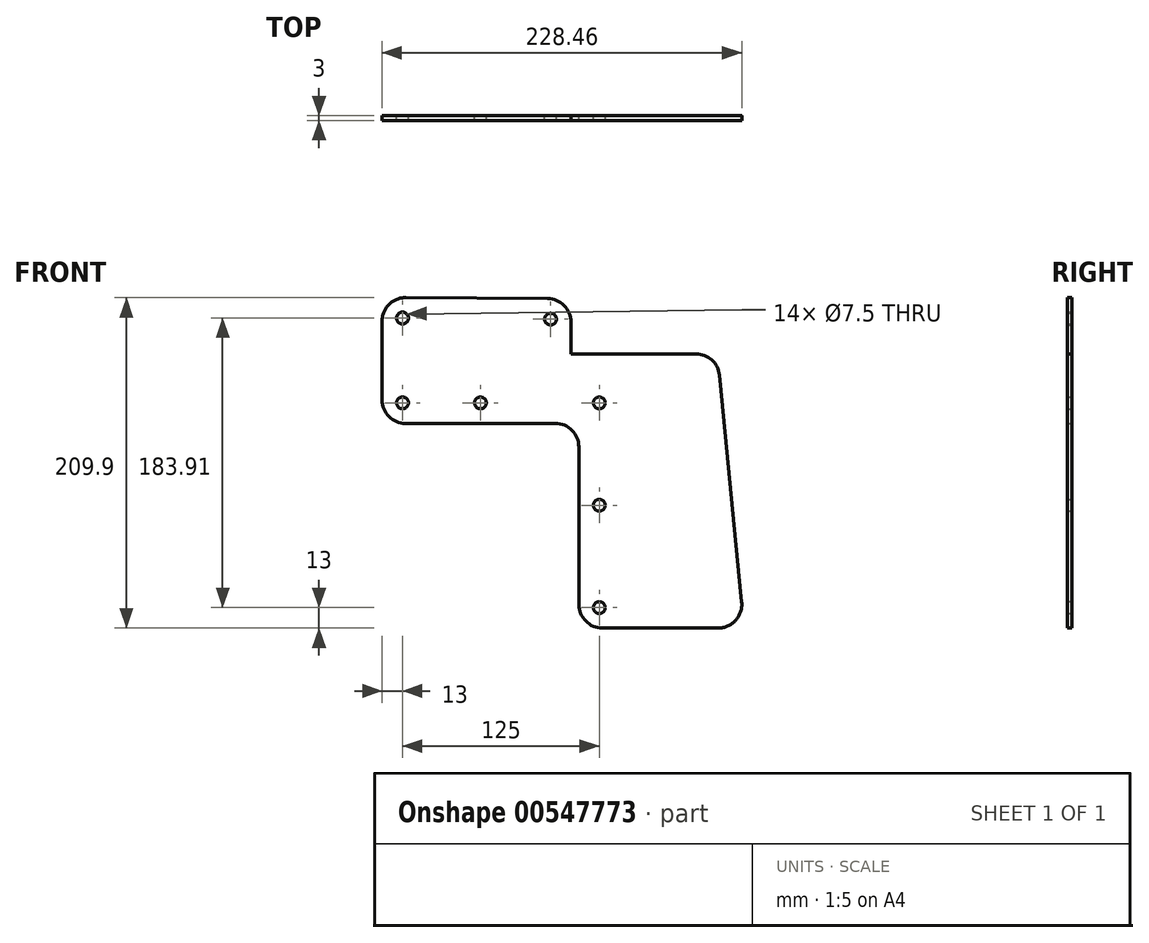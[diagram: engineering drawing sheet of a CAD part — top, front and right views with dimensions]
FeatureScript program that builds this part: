
annotation { "Feature Type Name" : "Feature", "Feature Type Description" : "" }
export const myFeature = defineFeature(function(context is Context, id is Id, definition is map)
    precondition{}
    {
        {
            var Q0;
            Q0=qCreatedBy(makeId("Front.planeOp"),FACE);
            var sketch = newSketch(context, id + "F0", { "sketchPlane" : qUnion([Q0])});
            skLineSegment(sketch, "E0", {"start": v(0, -15.1) * mm, "end": v(0, -65) * mm});
            skLineSegment(sketch, "E1", {"start": v(15, -80) * mm, "end": v(110, -80) * mm});
            skLineSegment(sketch, "E2", {"start": v(125, -95) * mm, "end": v(125, -195) * mm});
            skLineSegment(sketch, "E3", {"start": v(140, -210) * mm, "end": v(213.46, -210) * mm});
            skLineSegment(sketch, "E4", {"start": v(120, -15.72) * mm, "end": v(120, -35.83) * mm});
            skLineSegment(sketch, "E5", {"start": v(120, -35.83) * mm, "end": v(199.4, -35.83) * mm});
            skLineSegment(sketch, "E6", {"start": v(15.1, -0.1) * mm, "end": v(105.1, -0.73) * mm});
            skLineSegment(sketch, "E7", {"start": v(228.4, -193.54) * mm, "end": v(214.32, -49.37) * mm});
            skCircle(sketch, "E8", {"center": v(13, -13.1) * mm, "radius": 3.75 * mm});
            skCircle(sketch, "E9", {"center": v(107, -13.74) * mm, "radius": 3.75 * mm});
            skCircle(sketch, "E10", {"center": v(13, -67) * mm, "radius": 3.75 * mm});
            skCircle(sketch, "E11", {"center": v(138, -67) * mm, "radius": 3.75 * mm});
            skCircle(sketch, "E12", {"center": v(138, -197) * mm, "radius": 3.75 * mm});
            skCircle(sketch, "E13", {"center": v(138, -132) * mm, "radius": 3.75 * mm});
            skCircle(sketch, "E14", {"center": v(62.5, -67) * mm, "radius": 3.75 * mm});
            skPoint(sketch, "E14.centerSnap0", {"position": v(62.5, -80) * mm});
            skPoint(sketch, "E15.visualSharp", {"position": v(230, -210) * mm});
            skArc(sketch, "E15.filletArc", {"start": v(213.46, -210) * mm, "mid": v(224.57, -205.08) * mm, "end": v(228.4, -193.54) * mm});
            skPoint(sketch, "E16.visualSharp", {"position": v(213, -35.83) * mm});
            skArc(sketch, "E16.filletArc", {"start": v(214.32, -49.37) * mm, "mid": v(209.47, -39.72) * mm, "end": v(199.4, -35.83) * mm});
            skPoint(sketch, "E17.visualSharp", {"position": v(0, -80) * mm});
            skArc(sketch, "E17.filletArc", {"start": v(0, -65) * mm, "mid": v(4.4, -75.6) * mm, "end": v(15, -80) * mm});
            skPoint(sketch, "E18.visualSharp", {"position": v(125, -80) * mm});
            skArc(sketch, "E18.filletArc", {"start": v(125, -95) * mm, "mid": v(120.6, -84.4) * mm, "end": v(110, -80) * mm});
            skPoint(sketch, "E19.visualSharp", {"position": v(125, -210) * mm});
            skArc(sketch, "E19.filletArc", {"start": v(125, -195) * mm, "mid": v(129.4, -205.6) * mm, "end": v(140, -210) * mm});
            skPoint(sketch, "E20.visualSharp", {"position": v(120, -0.83) * mm});
            skArc(sketch, "E20.filletArc", {"start": v(120, -15.72) * mm, "mid": v(115.64, -5.15) * mm, "end": v(105.1, -0.73) * mm});
            skPoint(sketch, "E21.visualSharp", {"position": v(0, 0) * mm});
            skArc(sketch, "E21.filletArc", {"start": v(15.1, -0.1) * mm, "mid": v(4.43, -4.46) * mm, "end": v(0, -15.1) * mm});
            skSolve(sketch);
        }
        {
            var Q0;
            Q0=makeQuery(id+"F0.imprint","IMPRINT",FACE,{"disambiguationData":[TD([[makeQuery(id+"F0.imprint","IMPRINT",EDGE,{"derivedFrom":sQuery(id+"F0.wireOp",EDGE,"E0")}),1.0]])]});
            extrude(context, id + "F1", {"entities" : qUnion([Q0]), "depth" : 3 * mm, "offsetDistance" : 25 * mm});
        }
    });
